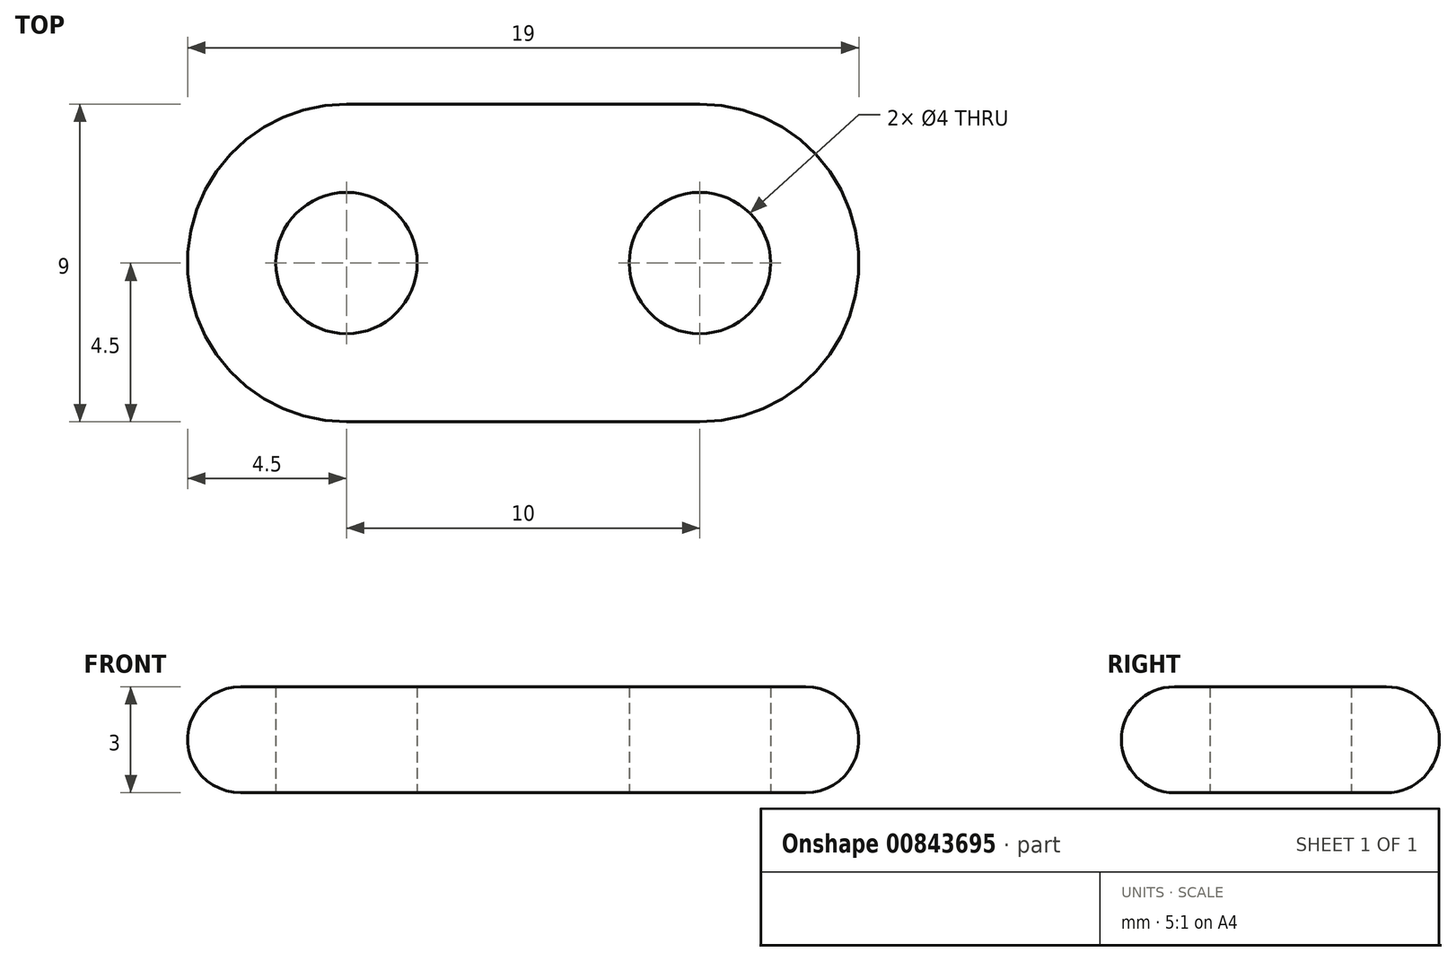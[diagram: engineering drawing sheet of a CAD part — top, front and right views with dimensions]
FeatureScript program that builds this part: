
annotation { "Feature Type Name" : "Feature", "Feature Type Description" : "" }
export const myFeature = defineFeature(function(context is Context, id is Id, definition is map)
    precondition{}
    {
        {
            var Q0;
            Q0=qCreatedBy(makeId("Top.planeOp"),FACE);
            var sketch = newSketch(context, id + "F0", { "sketchPlane" : qUnion([Q0])});
            skLineSegment(sketch, "E0.bottom", {"start": v(9.5, 4.5) * mm, "end": v(-9.5, 4.5) * mm});
            skLineSegment(sketch, "E0.top", {"start": v(9.5, -4.5) * mm, "end": v(-9.5, -4.5) * mm});
            skLineSegment(sketch, "E0.left", {"start": v(9.5, 4.5) * mm, "end": v(9.5, -4.5) * mm});
            skLineSegment(sketch, "E0.right", {"start": v(-9.5, 4.5) * mm, "end": v(-9.5, -4.5) * mm});
            skPoint(sketch, "E0.middle", {"position": v(0, 0) * mm});
            skCircle(sketch, "E1", {"center": v(-5, 0) * mm, "radius": 2 * mm});
            skCircle(sketch, "E2", {"center": v(5, 0) * mm, "radius": 2 * mm});
            skSolve(sketch);
        }
        {
            var Q0;
            Q0=makeQuery(id+"F0.imprint","IMPRINT",FACE,{"disambiguationData":[TD([[makeQuery(id+"F0.imprint","IMPRINT",EDGE,{"derivedFrom":sQuery(id+"F0.wireOp",EDGE,"E0.bottom")}),1.0]])]});
            extrude(context, id + "F1", {"entities" : qUnion([Q0]), "depth" : 3 * mm, "offsetDistance" : 25 * mm});
        }
        {
            var Q0;
            Q0=makeQuery(id+"F1.opExtrude","SWEPT_EDGE",EDGE,{"disambiguationData":[OSD([sQuery(id+"F0.wireOp",EDGE,"E0.top"),sQuery(id+"F0.wireOp",EDGE,"E0.right")])]});
            var Q1;
            Q1=makeQuery(id+"F1.opExtrude","SWEPT_EDGE",EDGE,{"disambiguationData":[OSD([sQuery(id+"F0.wireOp",EDGE,"E0.top"),sQuery(id+"F0.wireOp",EDGE,"E0.left")])]});
            var Q2;
            Q2=makeQuery(id+"F1.opExtrude","SWEPT_EDGE",EDGE,{"disambiguationData":[OSD([sQuery(id+"F0.wireOp",EDGE,"E0.bottom"),sQuery(id+"F0.wireOp",EDGE,"E0.left")])]});
            var Q3;
            Q3=makeQuery(id+"F1.opExtrude","SWEPT_EDGE",EDGE,{"disambiguationData":[OSD([sQuery(id+"F0.wireOp",EDGE,"E0.bottom"),sQuery(id+"F0.wireOp",EDGE,"E0.right")])]});
            fillet(context, id + "F2", {"entities" : qUnion([Q0, Q1, Q2, Q3]), "radius" : 4.5 * mm, "tangentPropagation" : true, "allowEdgeOverflow" : false});
        }
        {
            var Q0;
            Q0=makeQuery(id+"F1.opExtrude","CAP_EDGE",EDGE,{"disambiguationData":[OSD([sQuery(id+"F0.wireOp",EDGE,"E0.top")])],"isStart":false});
            var Q1;
            Q1=makeQuery(id+"F1.opExtrude","CAP_EDGE",EDGE,{"disambiguationData":[OSD([sQuery(id+"F0.wireOp",EDGE,"E0.bottom")])],"isStart":false});
            var Q2;
            Q2=makeQuery(id+"F1.opExtrude","CAP_EDGE",EDGE,{"disambiguationData":[OSD([sQuery(id+"F0.wireOp",EDGE,"E0.top")])],"isStart":true});
            fillet(context, id + "F3", {"entities" : qUnion([Q0, Q1, Q2]), "radius" : 1.5 * mm, "tangentPropagation" : true, "allowEdgeOverflow" : false});
        }
    });
